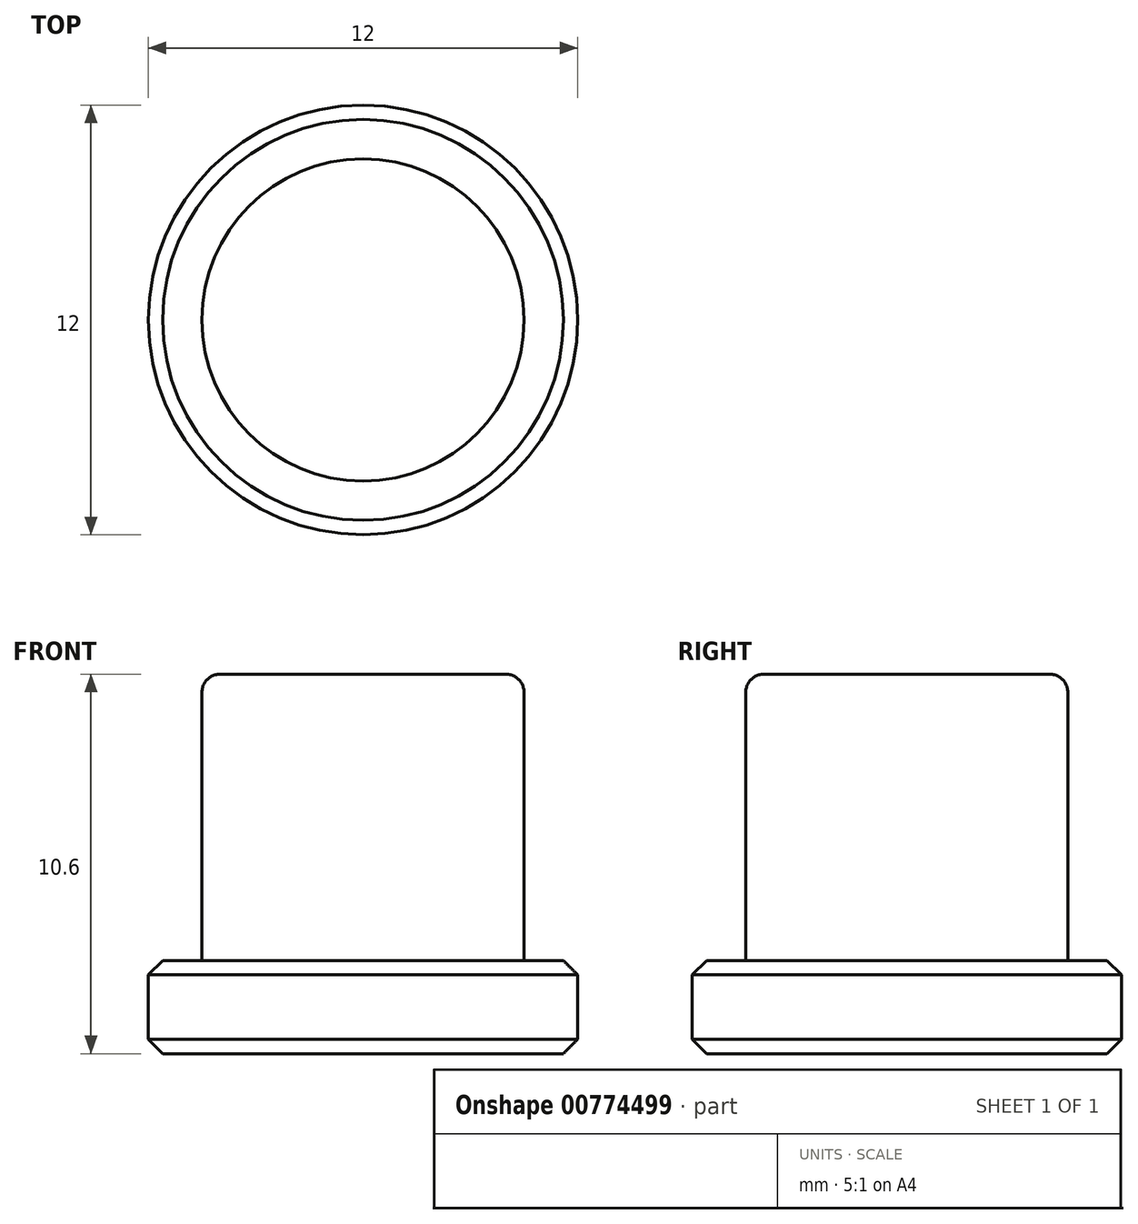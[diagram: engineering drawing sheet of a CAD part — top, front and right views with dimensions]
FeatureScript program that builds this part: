
annotation { "Feature Type Name" : "Feature", "Feature Type Description" : "" }
export const myFeature = defineFeature(function(context is Context, id is Id, definition is map)
    precondition{}
    {
        {
            var Q0;
            Q0=qCreatedBy(makeId("Top.planeOp"),FACE);
            var sketch = newSketch(context, id + "F0", { "sketchPlane" : qUnion([Q0])});
            skCircle(sketch, "E0", {"center": v(0, 0) * mm, "radius": 6 * mm});
            skSolve(sketch);
        }
        {
            var Q0;
            Q0 = qSketchRegion(id + "F0", true);
            extrude(context, id + "F1", {"entities" : qUnion([Q0]), "depth" : 2.6 * mm, "offsetDistance" : 25 * mm});
        }
        {
            var Q0;
            Q0=makeQuery(id+"F1.opExtrude","CAP_FACE",FACE,{"disambiguationData":[OSD([sQuery(id+"F0.wireOp",EDGE,"E0")])],"isStart":false});
            var sketch = newSketch(context, id + "F2", { "sketchPlane" : qUnion([Q0])});
            skCircle(sketch, "E1", {"center": v(0, 0) * mm, "radius": 4.5 * mm});
            skSolve(sketch);
        }
        {
            var Q0;
            Q0 = qSketchRegion(id + "F2", true);
            extrude(context, id + "F3", {"entities" : qUnion([Q0]), "operationType" : NewBodyOperationType.ADD, "flatOperationType" : FlatOperationType.REMOVE, "depth" : 8 * mm, "offsetDistance" : 25 * mm, "domain" : OperationDomain.MODEL});
        }
        {
            var Q0;
            Q0=makeQuery(id+"F3.opExtrude","CAP_EDGE",EDGE,{"disambiguationData":[OSD([sQuery(id+"F2.wireOp",EDGE,"E1")])],"isStart":false});
            fillet(context, id + "F4", {"entities" : qUnion([Q0]), "tangentPropagation" : true, "radius" : 0.5 * mm, "defaultsChanged" : true, "vertexSettings" : [], "allowEdgeOverflow" : false});
        }
        {
            var Q0;
            Q0=makeQuery(id+"F1.opExtrude","CAP_EDGE",EDGE,{"disambiguationData":[OSD([sQuery(id+"F0.wireOp",EDGE,"E0")])],"isStart":true});
            var Q1;
            Q1=makeQuery(id+"F1.opExtrude","CAP_EDGE",EDGE,{"disambiguationData":[OSD([sQuery(id+"F0.wireOp",EDGE,"E0")])],"isStart":false});
            chamfer(context, id + "F5", {"entities" : qUnion([Q0, Q1]), "width" : 0.4 * mm, "tangentPropagation" : true});
        }
    });
